# Revit family: BERS_65_COM_UN_Bticino Classe 300EOS Binnenpost_Legrand
name_source: partatom
category: Communication Devices
units: mm (PartAtom-declared; Revit-internal decimal feet)

## family parameters
Always vertical = No
Cut with Voids When Loaded = No
Maintain Annotation Orientation = No
Part Type = Normal
Room Calculation Point = No
Round Connector Dimension = Use Diameter
Shared = No
Work Plane-Based = No

## types (1)
- Classe 300EOS
    BERSnl_C_LE_Breedte = 121 mm  [stored 0.396982 ft]
    BERSnl_C_LE_Diepte = 32 mm  [stored 0.104987 ft]
    BERSnl_C_LE_Hoogte = 222 mm
    BERSnl_C_MA_Materiaal = BERSnl_FME_n6 PVC wit_Legrand
    BERSnl_C_MA_Materiaal01 = BERSnl_FME_o2 PVC wit_Legrand
    BERSnl_C_MA_Materiaal02 = BERSnl_FME_n6 PVC zwart_Legrand
    BERSnl_C_TX_CodeETIM = EC000779
    BERSnl_C_TX_CodeFabrikantGln = 541475999983
    BERSnl_C_TX_CodeGtin = 8005543677513
    BERSnl_C_TX_CodeProduct = BT-344842
    BERSnl_C_TX_CodeWaterdichtheidsklasse = 54
    BERSnl_C_TX_ContentCreator = DIBS42
    BERSnl_C_TX_ContentDatumUitgifte = 12-01-2021
    BERSnl_C_TX_Description = Legrand BTicino Classe 300 V13E binnenpost
    BERSnl_C_TX_Type = Communicatiesystemen
    BERSnl_C_UR_CodeETIM = https://prod.etim-international.com
    Camera = zonder camera
    Connector type = bus systeem
    Default Elevation = 0 mm  [stored 0 ft]
    Description = Legrand BTicino Classe 300 V13E binnenpost
    Deur open knop = Yes
    IfcDescription = Legrand BTicino Classe 300 V13E binnenpost
    IfcExportAs = IfcAudioVisualApplianceType
    IfcExportType = TELEPHONE
    Installatie methode = opbouw
    Interface type = Wi-Fi/ RJ45
    Manufacturer = Legrand
    Met video = Yes
    Model = Class 300 V13E
    Operating temperature MIN-MAX = +5/+40 °C
    Scherm grootte (inch) = 5
    Scherm resolutie = 1280x720
    Touchscreen = Yes
    URL = https://ecataleg.be

note: [stored X ft] marks values corroborated as IEEE doubles in the binary element streams (Revit-internal decimal feet)

## geometry (parser evidence)
native form markers: Sweep x3
no freeform markers — native parametric forms only
